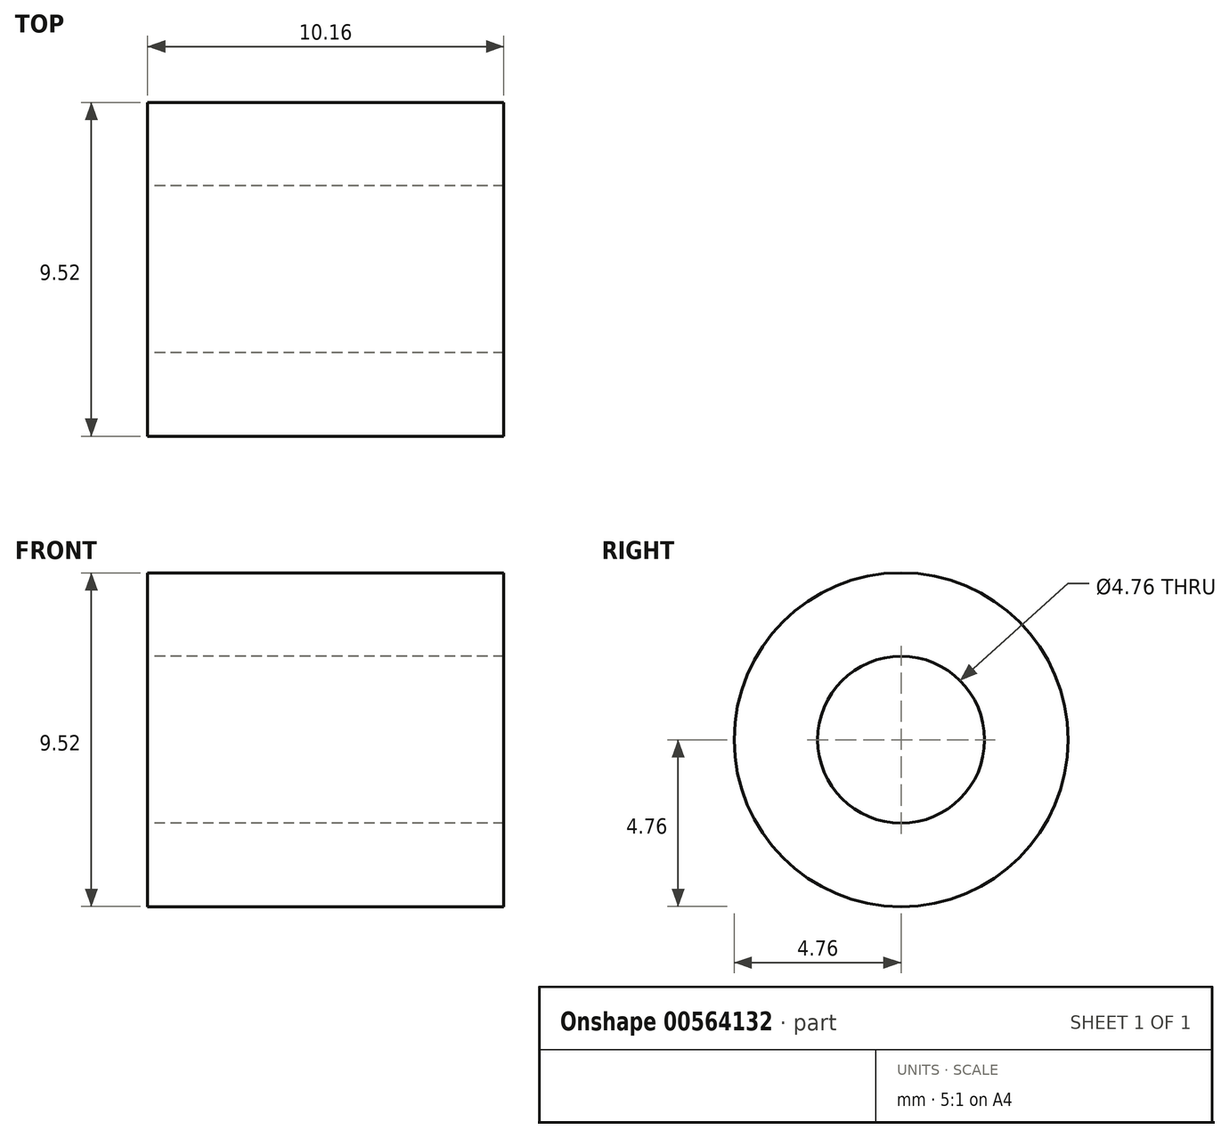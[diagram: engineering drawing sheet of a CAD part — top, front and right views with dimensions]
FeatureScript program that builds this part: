
annotation { "Feature Type Name" : "Feature", "Feature Type Description" : "" }
export const myFeature = defineFeature(function(context is Context, id is Id, definition is map)
    precondition{}
    {
        {
            var Q0;
            Q0=qCreatedBy(makeId("Right.planeOp"),FACE);
            var sketch = newSketch(context, id + "F0", { "sketchPlane" : qUnion([Q0])});
            skCircle(sketch, "E0", {"center": v(0, 0) * mm, "radius": 4.76 * mm});
            skCircle(sketch, "E1", {"center": v(0, 0) * mm, "radius": 2.38 * mm});
            skSolve(sketch);
        }
        {
            var Q0;
            Q0=qSketchRegion(id+"F0",true);
            extrude(context, id + "F1", {"entities" : qUnion([Q0]), "depth" : 10.16 * mm, "offsetDistance" : 25.4 * mm});
        }
    });
